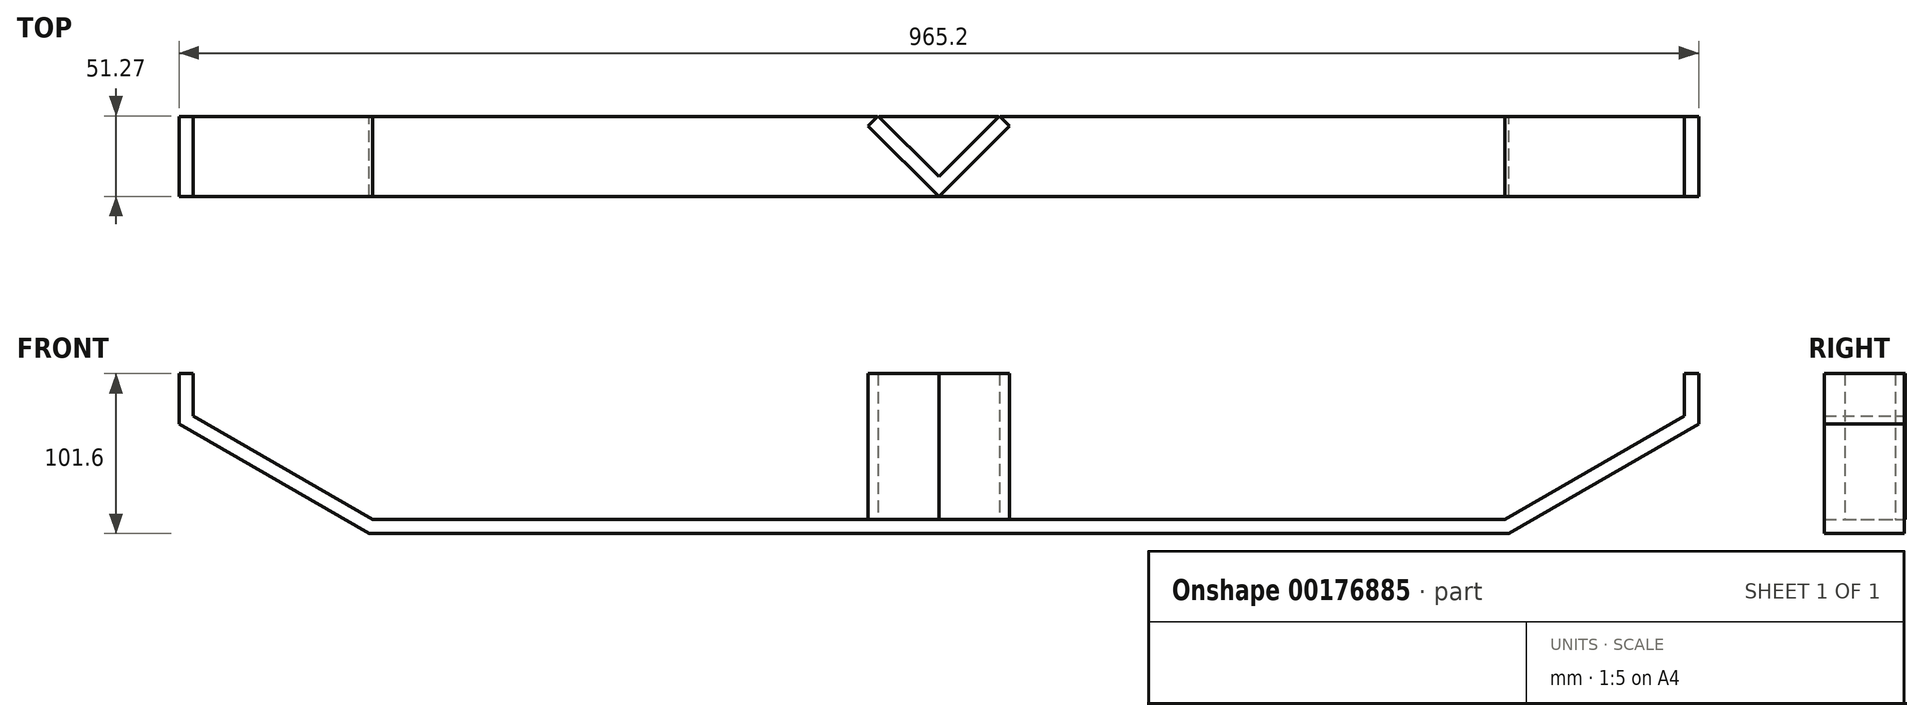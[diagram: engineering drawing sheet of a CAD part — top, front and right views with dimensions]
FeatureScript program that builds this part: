
annotation { "Feature Type Name" : "Feature", "Feature Type Description" : "" }
export const myFeature = defineFeature(function(context is Context, id is Id, definition is map)
    precondition{}
    {
        {
            var Q0;
            Q0=qCreatedBy(makeId("Front.planeOp"),FACE);
            var sketch = newSketch(context, id + "F0", { "sketchPlane" : qUnion([Q0])});
            skLineSegment(sketch, "E0", {"start": v(0, 0) * mm, "end": v(723.9, 0) * mm});
            skLineSegment(sketch, "E1.0", {"start": v(844.55, 69.66) * mm, "end": v(844.55, 101.6) * mm});
            skLineSegment(sketch, "E2", {"start": v(723.9, 0) * mm, "end": v(844.55, 69.66) * mm});
            skLineSegment(sketch, "E3", {"start": v(361.95, 0) * mm, "end": v(361.95, 114.97) * mm});
            skLineSegment(sketch, "E4.MirrorCS", {"start": v(0, 0) * mm, "end": v(-120.65, 69.66) * mm});
            skLineSegment(sketch, "E5.MirrorCS", {"start": v(-120.65, 69.66) * mm, "end": v(-120.65, 101.6) * mm});
            skLineSegment(sketch, "E6.0", {"start": v(-111.65, 74.85) * mm, "end": v(-111.65, 101.6) * mm});
            skLineSegment(sketch, "E7.0", {"start": v(2.41, 9) * mm, "end": v(-111.65, 74.85) * mm});
            skLineSegment(sketch, "E8.0", {"start": v(2.41, 9) * mm, "end": v(721.49, 9) * mm});
            skLineSegment(sketch, "E9.0", {"start": v(721.49, 9) * mm, "end": v(835.55, 74.85) * mm});
            skLineSegment(sketch, "E10.0", {"start": v(835.55, 74.85) * mm, "end": v(835.55, 101.6) * mm});
            skLineSegment(sketch, "E11.filletArc", {"start": v(835.55, 74.85) * mm, "end": v(835.55, 74.85) * mm});
            skLineSegment(sketch, "E12.filletArc", {"start": v(721.49, 9) * mm, "end": v(721.49, 9) * mm});
            skLineSegment(sketch, "E13.filletArc", {"start": v(2.41, 9) * mm, "end": v(2.41, 9) * mm});
            skLineSegment(sketch, "E14.filletArc", {"start": v(-111.65, 74.85) * mm, "end": v(-111.65, 74.85) * mm});
            skLineSegment(sketch, "E15", {"start": v(844.55, 101.6) * mm, "end": v(835.55, 101.6) * mm});
            skLineSegment(sketch, "E16.filletArc", {"start": v(835.55, 101.6) * mm, "end": v(835.55, 101.6) * mm});
            skLineSegment(sketch, "E17", {"start": v(-120.65, 101.6) * mm, "end": v(-111.65, 101.6) * mm});
            skLineSegment(sketch, "E18.filletArc", {"start": v(-111.65, 101.6) * mm, "end": v(-111.65, 101.6) * mm});
            skSolve(sketch);
        }
        {
            var Q0;
            Q0=qCreatedBy(makeId("Top.planeOp"),FACE);
            var sketch = newSketch(context, id + "F1", { "sketchPlane" : qUnion([Q0])});
            skLineSegment(sketch, "E19", {"start": v(497.53, 179.1) * mm, "end": v(542.43, 224) * mm});
            skLineSegment(sketch, "E20", {"start": v(497.53, 179.1) * mm, "end": v(452.63, 224) * mm});
            skLineSegment(sketch, "E21.0", {"start": v(497.53, 191.83) * mm, "end": v(536.07, 230.37) * mm});
            skLineSegment(sketch, "E22", {"start": v(542.43, 224) * mm, "end": v(536.07, 230.37) * mm});
            skLineSegment(sketch, "E23.0", {"start": v(497.53, 191.83) * mm, "end": v(459, 230.37) * mm});
            skLineSegment(sketch, "E24", {"start": v(452.63, 224) * mm, "end": v(459, 230.37) * mm});
            skSolve(sketch);
        }
        {
            var Q0;
            Q0=makeQuery(id+"F1.imprint","IMPRINT",FACE,{"disambiguationData":[TD([[makeQuery(id+"F1.imprint","IMPRINT",EDGE,{"derivedFrom":sQuery(id+"F1.wireOp",EDGE,"E19")}),1.0]])]});
            extrude(context, id + "F2", {"entities" : qUnion([Q0]), "depth" : 92.6 * mm});
        }
        {
            var Q0;
            {var subQ0=sQuery(id+"F0.wireOp",EDGE,"E4.MirrorCS");Q0=makeQuery(id+"F0.imprint","IMPRINT",FACE,{"disambiguationData":[TD([[makeQuery(id+"F0.imprint","IMPRINT",EDGE,{"derivedFrom":subQ0}),-1.0]])]});}
            var Q1;
            Q1=makeQuery(id+"F0.imprint","IMPRINT",FACE,{"disambiguationData":[TD([[makeQuery(id+"F0.imprint","IMPRINT",EDGE,{"derivedFrom":sQuery(id+"F0.wireOp",EDGE,"E1.0")}),1.0]])]});
            extrude(context, id + "F3", {"entities" : qUnion([Q0, Q1]), "depth" : 50.8 * mm});
        }
        {
            var Q0;
            Q0=makeQuery(id+"F3.opExtrude","CAP_EDGE",EDGE,{"disambiguationData":[OSD([sQuery(id+"F0.wireOp",EDGE,"E8.0")])],"isStart":false});
            cPoint(context, id + "F4", {"entities" : qUnion([Q0]), "parameter" : 0.5});
        }
        {
            var Q0;
            Q0=makeQuery(id+"F2.opExtrude","SWEPT_BODY",BODY,{"disambiguationData":[OSD([sQuery(id+"F1.wireOp",EDGE,"E19"),sQuery(id+"F1.wireOp",EDGE,"E20"),sQuery(id+"F1.wireOp",EDGE,"E21.0"),sQuery(id+"F1.wireOp",EDGE,"E22"),sQuery(id+"F1.wireOp",EDGE,"E23.0"),sQuery(id+"F1.wireOp",EDGE,"E24")])]});
            var Q1;
            Q1=sQuery(id+"F1.wireOp",VERTEX,"E19.start");
            var Q2;
            Q2 = qCreatedBy(id + "F4" ,VERTEX);
            transform(context, id + "F5", {"entities" : qUnion([Q0]), "transformType" : TransformType.TRANSLATION_ENTITY, "oppositeDirectionEntity" : false, "transformLine" : qUnion([Q1, Q2]), "makeCopy" : false});
        }
    });
